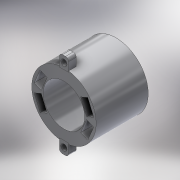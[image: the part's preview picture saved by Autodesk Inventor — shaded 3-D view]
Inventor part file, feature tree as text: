
AUTODESK INVENTOR PART (.ipt)
format: ipt  version: 2018 (Build 220112000, 112)  size: 157,184 bytes
history: native  units: in
note: dims shown in document units (in); Inventor stores cm internally (conversion verified against a paired STEP export)
features: fillet x1
ambient origin geometry x8: Origin, YZ Plane, XZ Plane, XY Plane, X Axis, Y Axis, Z Axis, Center Point
bodies: Solid1 (feature_tree)
feature tree (1):
  fillet  "Fillet2"  [1 undecoded]
note: 1 required parameter value undecoded (feature->parameter linkage not recoverable at this tier; creation-order binding heuristic only, values carry confidence <= 0.55)
